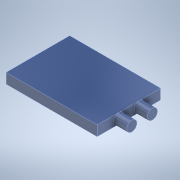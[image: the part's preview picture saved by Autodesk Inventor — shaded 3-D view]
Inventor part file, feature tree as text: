
AUTODESK INVENTOR PART (.ipt)
format: ipt  version: 2021 (Build 250183000, 183)  size: 112,640 bytes
history: native  units: mm
features: extrude x2, sketch x2
ambient origin geometry x8: Origin, YZ Plane, XZ Plane, XY Plane, X Axis, Y Axis, Z Axis, Center Point
bodies: Solid1 (feature_tree)
feature tree (4):
  extrude  "Extrusion1"  Depth=43.3mm
  extrude  "Extrusion2"  Depth=7.0mm
  sketch  "Sketch1"  dims[d0=62.0mm d1=43.3mm]
  sketch  "Sketch2"  dims[d2=7.0mm d3=0.0mm d4=7.0mm d5=7.0mm d6=14.0mm d7=7.0mm d8=9.0mm d9=0.0mm]
